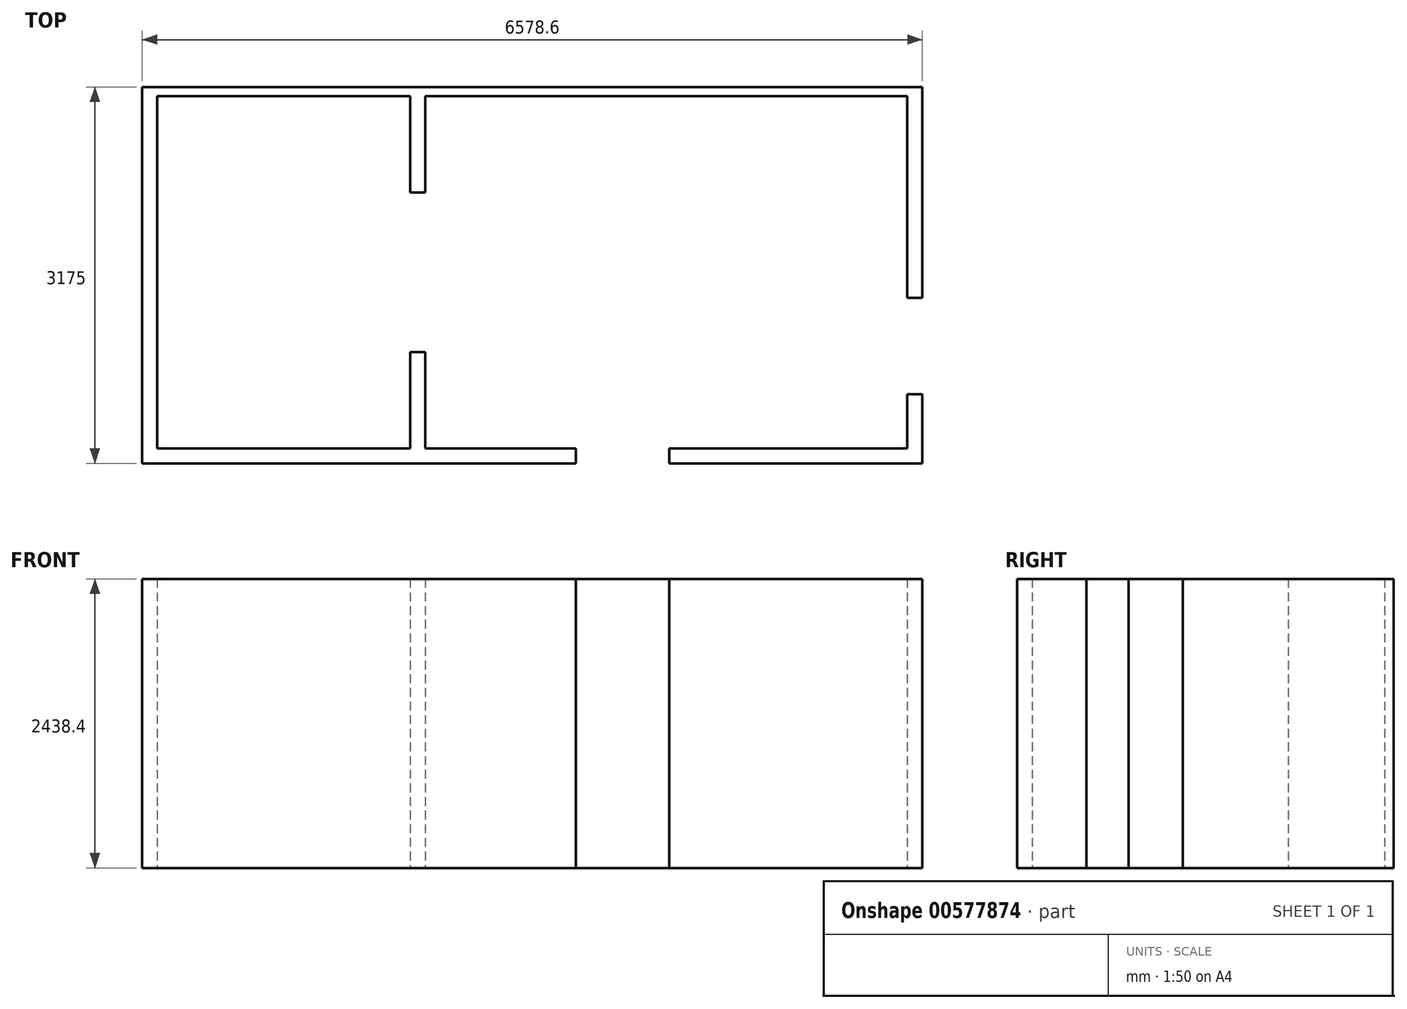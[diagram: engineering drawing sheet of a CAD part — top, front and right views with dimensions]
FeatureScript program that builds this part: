
annotation { "Feature Type Name" : "Feature", "Feature Type Description" : "" }
export const myFeature = defineFeature(function(context is Context, id is Id, definition is map)
    precondition{}
    {
        {
            var Q0;
            Q0=qCreatedBy(makeId("Top.planeOp"),FACE);
            var sketch = newSketch(context, id + "F0", { "sketchPlane" : qUnion([Q0])});
            skLineSegment(sketch, "E0", {"start": v(-3487.41, -586.9) * mm, "end": v(-2217.41, -586.9) * mm});
            skLineSegment(sketch, "E1", {"start": v(-2217.41, -586.9) * mm, "end": v(-2217.41, -713.9) * mm});
            skLineSegment(sketch, "E2", {"start": v(-2217.41, -713.9) * mm, "end": v(-1430.01, -713.9) * mm});
            skLineSegment(sketch, "E3", {"start": v(-1430.01, -713.9) * mm, "end": v(-1430.01, -586.9) * mm});
            skLineSegment(sketch, "E4", {"start": v(-1430.01, -586.9) * mm, "end": v(576.59, -586.9) * mm});
            skLineSegment(sketch, "E5", {"start": v(576.59, -586.9) * mm, "end": v(576.59, -129.7) * mm});
            skLineSegment(sketch, "E6", {"start": v(576.59, -129.7) * mm, "end": v(703.59, -129.7) * mm});
            skLineSegment(sketch, "E7", {"start": v(703.59, -713.9) * mm, "end": v(703.59, 2461.1) * mm});
            skLineSegment(sketch, "E8", {"start": v(703.59, 683.1) * mm, "end": v(576.59, 683.1) * mm});
            skLineSegment(sketch, "E9", {"start": v(576.59, 683.1) * mm, "end": v(576.59, 2384.9) * mm});
            skLineSegment(sketch, "E10", {"start": v(576.59, 2384.9) * mm, "end": v(-3487.41, 2384.9) * mm});
            skLineSegment(sketch, "E11", {"start": v(-3487.41, 2384.9) * mm, "end": v(-3487.41, 1572.1) * mm});
            skLineSegment(sketch, "E12", {"start": v(-3614.41, 2384.9) * mm, "end": v(-3614.41, 1572.1) * mm});
            skLineSegment(sketch, "E13", {"start": v(-3614.41, -586.9) * mm, "end": v(-5748.01, -586.9) * mm});
            skLineSegment(sketch, "E14", {"start": v(-3614.41, 2384.9) * mm, "end": v(-5748.01, 2384.9) * mm});
            skLineSegment(sketch, "E15", {"start": v(-5875.01, -713.9) * mm, "end": v(-5875.01, 2461.1) * mm});
            skLineSegment(sketch, "E16", {"start": v(-5748.01, -586.9) * mm, "end": v(-5748.01, 2384.9) * mm});
            skLineSegment(sketch, "E17", {"start": v(-5875.01, 2461.1) * mm, "end": v(703.59, 2461.1) * mm});
            skLineSegment(sketch, "E18", {"start": v(-5875.01, -713.9) * mm, "end": v(703.59, -713.9) * mm});
            skLineSegment(sketch, "E19", {"start": v(-3614.41, 225.9) * mm, "end": v(-3487.41, 225.9) * mm});
            skLineSegment(sketch, "E20", {"start": v(-3614.41, 1572.1) * mm, "end": v(-3487.41, 1572.1) * mm});
            skLineSegment(sketch, "E21.trimOffspring", {"start": v(-3614.41, 225.9) * mm, "end": v(-3614.41, -586.9) * mm});
            skLineSegment(sketch, "E22.trimOffspring", {"start": v(-3487.41, 225.9) * mm, "end": v(-3487.41, -586.9) * mm});
            skPoint(sketch, "E23.end.orphan", {"position": v(-5748.01, -586.9) * mm});
            skSolve(sketch);
        }
        {
            var Q0;
            Q0=makeQuery(id+"F0.imprint","IMPRINT",FACE,{"disambiguationData":[TD([[makeQuery(id+"F0.imprint","IMPRINT",EDGE,{"derivedFrom":sQuery(id+"F0.wireOp",EDGE,"E0")}),-1.0]])]});
            var Q1;
            {var subQ1=sQuery(id+"F0.wireOp",EDGE,"E3");Q1=makeQuery(id+"F0.imprint","IMPRINT",FACE,{"disambiguationData":[TD([[makeQuery(id+"F0.imprint","IMPRINT",EDGE,{"derivedFrom":subQ1}),-1.0]])]});}
            extrude(context, id + "F1", {"entities" : qUnion([Q0, Q1]), "depth" : 2438.4 * mm, "offsetDistance" : 25.4 * mm});
        }
    });
